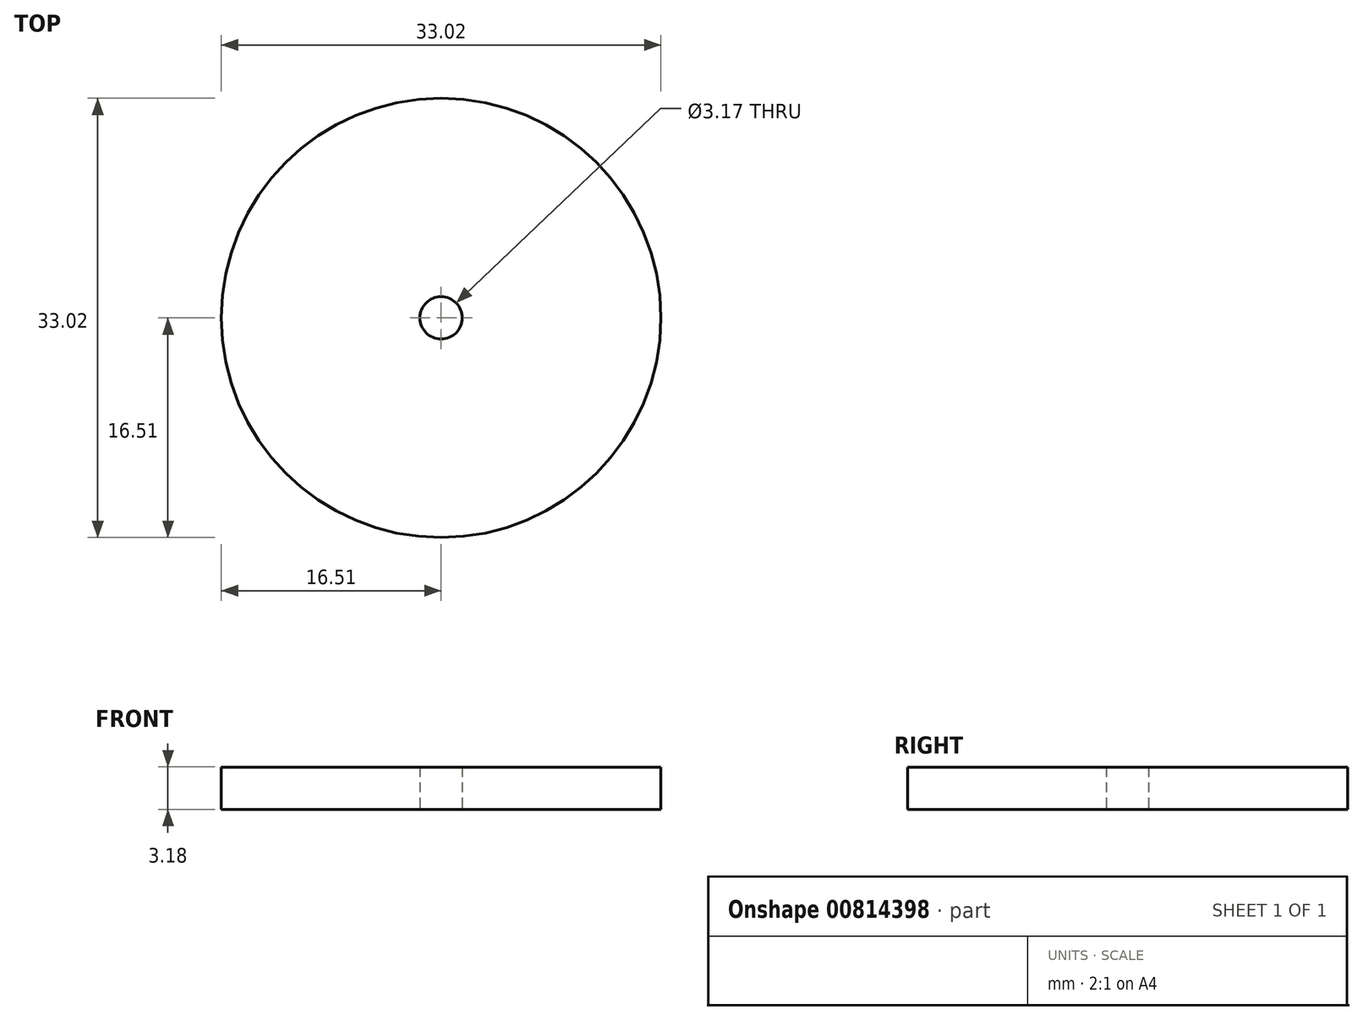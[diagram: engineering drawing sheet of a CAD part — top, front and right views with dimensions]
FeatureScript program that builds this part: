
annotation { "Feature Type Name" : "Feature", "Feature Type Description" : "" }
export const myFeature = defineFeature(function(context is Context, id is Id, definition is map)
    precondition{}
    {
        {
            var Q0;
            Q0=qCreatedBy(makeId("Top.planeOp"),FACE);
            var sketch = newSketch(context, id + "F0", { "sketchPlane" : qUnion([Q0])});
            skCircle(sketch, "E0", {"center": v(0, 0) * mm, "radius": 1.59 * mm});
            skCircle(sketch, "E1", {"center": v(0, 0) * mm, "radius": 16.51 * mm});
            skSolve(sketch);
        }
        {
            var Q0;
            Q0=makeQuery(id+"F0.imprint","IMPRINT",FACE,{"disambiguationData":[TD([[makeQuery(id+"F0.imprint","IMPRINT",EDGE,{"derivedFrom":sQuery(id+"F0.wireOp",EDGE,"E0")}),-1.0]])]});
            extrude(context, id + "F1", {"entities" : qUnion([Q0]), "depth" : 3.17 * mm, "offsetDistance" : 25.4 * mm});
        }
    });
